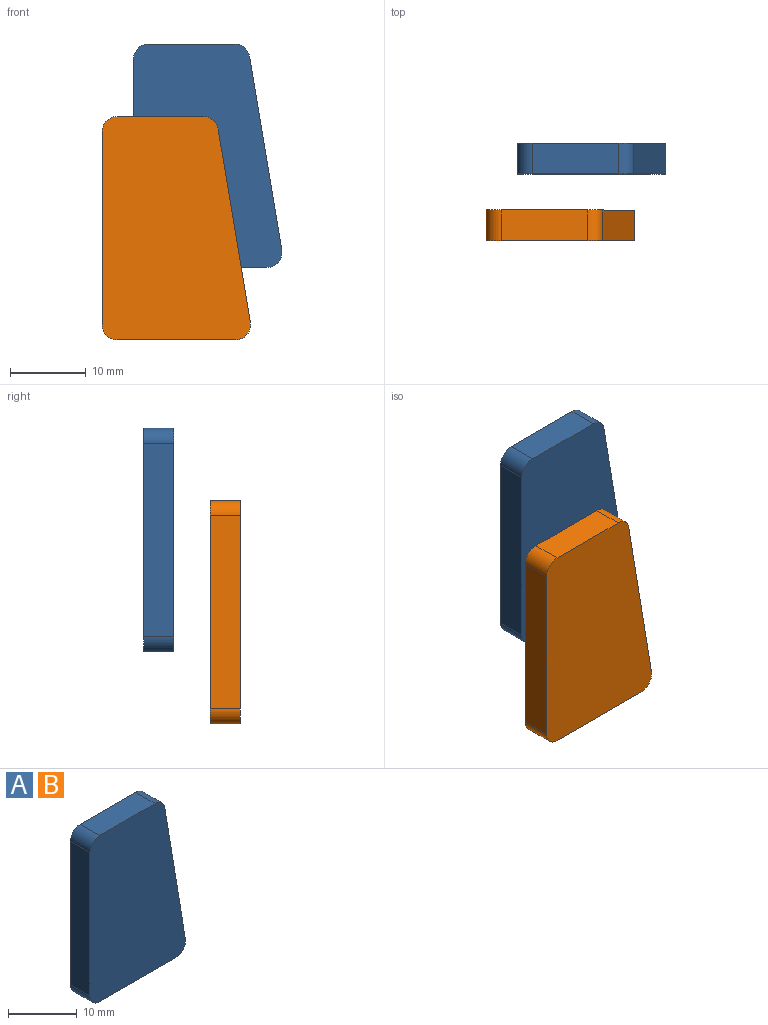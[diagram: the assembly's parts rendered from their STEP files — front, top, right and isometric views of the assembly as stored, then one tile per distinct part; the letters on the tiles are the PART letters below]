
ASSEMBLY  parts=2 mates=1
PART A: 10 faces, bbox 19.6x4x29.5 mm
  f0: plane 25.55x4mm, normal (-1,0,0), area 102.2mm2, adj f1,f7,f8,f9
  f1: cylinder r=2mm len=4mm, axis (0,1,0), area 12.6mm2, adj f0,f2,f8,f9
  f2: plane 15.64x4mm, normal (0,0,-1), area 62.6mm2, adj f1,f3,f8,f9
  f3: cylinder r=2mm len=4mm, axis (0,1,0), area 13.9mm2, adj f2,f4,f8,f9
  f4: plane 25.55x4.26mm, normal (0.99,0,0.16), area 103.6mm2, adj f3,f5,f8,f9
  f5: cylinder r=2mm len=4mm, axis (0,1,0), area 11.2mm2, adj f4,f6,f8,f9
  f6: plane 11.38x4mm, normal (0,0,1), area 45.5mm2, adj f5,f7,f8,f9
  f7: cylinder r=2mm len=4mm, axis (0,1,0), area 12.6mm2, adj f0,f6,f8,f9
  f8: plane 29.55x19.64mm, normal (0,-1,0), area 514.6mm2, adj f0,f1,f2,f3,f4,f5,f6,f7
  f9: plane 29.55x19.64mm, normal (0,1,0), area 514.6mm2, adj f0,f1,f2,f3,f4,f5,f6,f7
PART B: same geometry as A
PLACE A t=(-16.68,9.22,2.01)mm
PLACE B t=(-20.84,0.43,-7.58)mm
MATE parallel B.f6 <-> A.f6  axis (0,0,1) through (-13.68,-1.57,22.42)mm
